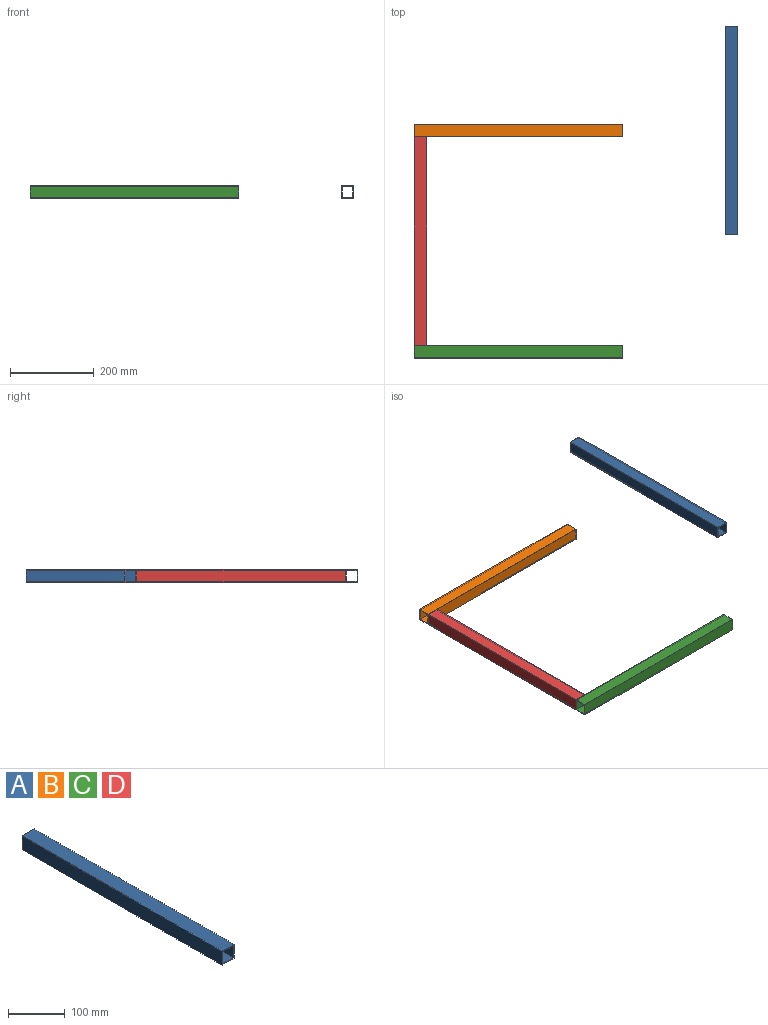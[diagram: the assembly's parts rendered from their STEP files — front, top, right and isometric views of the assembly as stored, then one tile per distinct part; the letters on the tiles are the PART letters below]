
ASSEMBLY  parts=4 mates=1
PART A: 10 faces, bbox 30x500x30 mm
  f0: plane 30x30mm, normal (0,-1,0), area 224mm2, adj f2,f3,f4,f5,f6,f7,f8,f9
  f1: plane 30x30mm, normal (0,1,0), area 224mm2, adj f2,f3,f4,f5,f6,f7,f8,f9
  f2: plane 500x30mm, normal (-1,0,0), area 15000mm2, adj f0,f1,f3,f5
  f3: plane 500x30mm, normal (0,0,-1), area 15000mm2, adj f0,f1,f2,f4
  f4: plane 500x30mm, normal (1,0,0), area 15000mm2, adj f0,f1,f3,f5
  f5: plane 500x30mm, normal (0,0,1), area 15000mm2, adj f0,f1,f2,f4
  f6: plane 500x26mm, normal (1,0,0), area 13000mm2, adj f0,f1,f7,f9
  f7: plane 500x26mm, normal (0,0,1), area 13000mm2, adj f0,f1,f6,f8
  f8: plane 500x26mm, normal (-1,0,0), area 13000mm2, adj f0,f1,f7,f9
  f9: plane 500x26mm, normal (0,0,-1), area 13000mm2, adj f0,f1,f6,f8
PART B: same geometry as A
PART C: same geometry as A
PART D: same geometry as A
PLACE A t=(745,265,0)mm
PLACE B rot(axis=(0.71,-0.71,0),180deg) t=(220,250,30)mm fixed
PLACE C rot(axis=(0,0,-1),90deg) t=(220,-280,0)mm fixed
PLACE D at identity fixed
MATE planar A.f5 <-> B.f3  axis (0,0,1) through (730,265,30)mm
